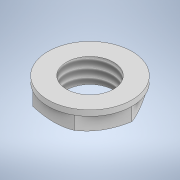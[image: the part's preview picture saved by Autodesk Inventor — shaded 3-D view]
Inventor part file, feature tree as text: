
AUTODESK INVENTOR PART (.ipt)
format: ipt  version: 2021 (Build 250183000, 183)  size: 141,824 bytes
history: native  units: mm
features: sketch x4, extrude x2, revolve x1, hole x1, projected_geometry x1
ambient origin geometry x8: Origin, YZ Plane, XZ Plane, XY Plane, X Axis, Y Axis, Z Axis, Center Point
bodies: Solid1 (feature_tree)
feature tree (9):
  extrude  "Extrusion1"  Depth=4.0mm TaperAngle=0.0deg
  extrude  "Extrusion2"  TaperAngle=60.0deg  [1 undecoded]
  revolve  "Revolution1"  [1 undecoded]
  hole  "Hole1"  [1 undecoded]
  sketch  "Sketch1"  dims[d0=15.6mm d1=4.0mm d2=0.0mm]
  sketch  "Sketch2"  dims[d3=1.2mm d4=0.0mm d5=60.0deg]
  projected_geometry  "Projected Loop1"
  sketch  "Sketch3"  dims[d6=5.2mm d7=4.0mm]
  sketch  "Sketch4"  dims[d8=90.0deg d9=10.106mm d10=8.5mm d11=4.0mm d12=2.0mm d13=90.0deg d14=8.5mm d15=20.594885mm]
note: 3 required parameter values undecoded (feature->parameter linkage not recoverable at this tier; creation-order binding heuristic only, values carry confidence <= 0.55)